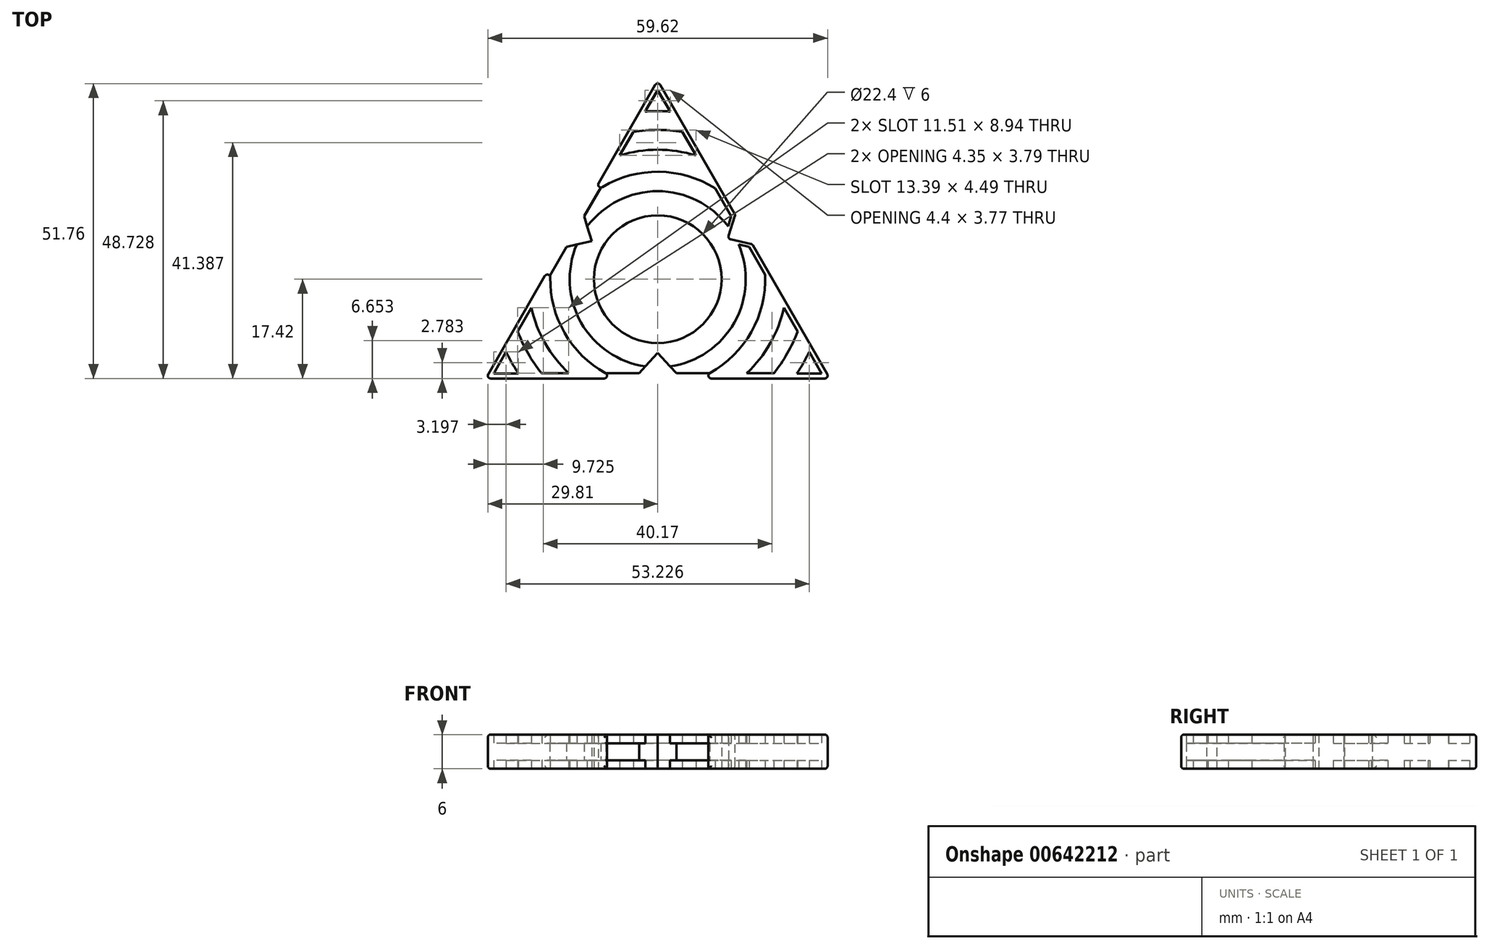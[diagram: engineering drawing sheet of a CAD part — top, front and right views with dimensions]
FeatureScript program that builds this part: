
annotation { "Feature Type Name" : "Feature", "Feature Type Description" : "" }
export const myFeature = defineFeature(function(context is Context, id is Id, definition is map)
    precondition{}
    {
        {
            var Q0;
            Q0=qCreatedBy(makeId("Top.planeOp"),FACE);
            var sketch = newSketch(context, id + "F0", { "sketchPlane" : qUnion([Q0])});
            skPoint(sketch, "E0.0.midPoint", {"position": v(0, -17.42) * mm});
            skLineSegment(sketch, "E1", {"start": v(-12.28, 7.1) * mm, "end": v(-16.57, 6.15) * mm});
            skLineSegment(sketch, "E2", {"start": v(-3.29, -17.42) * mm, "end": v(0, -13.75) * mm});
            skLineSegment(sketch, "E3.MirrorCS", {"start": v(3.29, -17.42) * mm, "end": v(0, -13.75) * mm});
            skLineSegment(sketch, "E4.MirrorCS", {"start": v(-12.28, 7.1) * mm, "end": v(-13.61, 11.27) * mm});
            skLineSegment(sketch, "E5.MirrorCS", {"start": v(12.28, 7.1) * mm, "end": v(16.57, 6.15) * mm});
            skLineSegment(sketch, "E6.MirrorCS", {"start": v(12.28, 7.1) * mm, "end": v(13.61, 11.27) * mm});
            skLineSegment(sketch, "E7", {"start": v(-16.57, 6.15) * mm, "end": v(-30.18, -17.42) * mm});
            skLineSegment(sketch, "E8", {"start": v(-13.61, 11.27) * mm, "end": v(-12.28, 7.1) * mm});
            skLineSegment(sketch, "E9", {"start": v(-16.57, 6.15) * mm, "end": v(-12.28, 7.1) * mm});
            skLineSegment(sketch, "E10", {"start": v(-13.61, 11.27) * mm, "end": v(0, 34.84) * mm});
            skLineSegment(sketch, "E11", {"start": v(0, 34.84) * mm, "end": v(13.61, 11.27) * mm});
            skLineSegment(sketch, "E12", {"start": v(16.57, 6.15) * mm, "end": v(30.18, -17.42) * mm});
            skLineSegment(sketch, "E13", {"start": v(30.18, -17.42) * mm, "end": v(3.29, -17.42) * mm});
            skLineSegment(sketch, "E14", {"start": v(0, -13.75) * mm, "end": v(-3.29, -17.42) * mm});
            skLineSegment(sketch, "E15", {"start": v(-3.29, -17.42) * mm, "end": v(-30.18, -17.42) * mm});
            skCircle(sketch, "E16", {"center": v(0, 0) * mm, "radius": 11.2 * mm});
            skLineSegment(sketch, "E17", {"start": v(-11.57, 6.62) * mm, "end": v(-12.9, 11.08) * mm});
            skLineSegment(sketch, "E18", {"start": v(-12.9, 11.08) * mm, "end": v(0, 33.2) * mm});
            skLineSegment(sketch, "E19.MirrorCS", {"start": v(-11.5, 6.73) * mm, "end": v(-16.03, 5.67) * mm});
            skLineSegment(sketch, "E20.MirrorCS", {"start": v(-16.03, 5.67) * mm, "end": v(-28.79, -16.53) * mm});
            skLineSegment(sketch, "E21", {"start": v(0, -12.94) * mm, "end": v(-3.26, -16.5) * mm});
            skLineSegment(sketch, "E22", {"start": v(-3.26, -16.5) * mm, "end": v(-28.79, -16.53) * mm});
            skLineSegment(sketch, "E23", {"start": v(0, 37.15) * mm, "end": v(0, -20.14) * mm, "construction": true});
            skLineSegment(sketch, "E24.MirrorCS", {"start": v(12.9, 11.08) * mm, "end": v(0, 33.2) * mm});
            skLineSegment(sketch, "E25.MirrorCS", {"start": v(11.57, 6.62) * mm, "end": v(12.9, 11.08) * mm});
            skLineSegment(sketch, "E26.MirrorCS", {"start": v(11.5, 6.73) * mm, "end": v(16.03, 5.67) * mm});
            skLineSegment(sketch, "E27.MirrorCS", {"start": v(16.03, 5.67) * mm, "end": v(28.79, -16.53) * mm});
            skLineSegment(sketch, "E28.MirrorCS", {"start": v(3.26, -16.5) * mm, "end": v(28.79, -16.53) * mm});
            skLineSegment(sketch, "E29.MirrorCS", {"start": v(0, -12.94) * mm, "end": v(3.26, -16.5) * mm});
            skCircle(sketch, "E30", {"center": v(0, 0) * mm, "radius": 15.45 * mm});
            skCircle(sketch, "E31", {"center": v(0, 0) * mm, "radius": 18.86 * mm});
            skCircle(sketch, "E32", {"center": v(0, 0) * mm, "radius": 22.73 * mm});
            skCircle(sketch, "E33", {"center": v(0, 0) * mm, "radius": 26.21 * mm});
            skCircle(sketch, "E34", {"center": v(0, 0) * mm, "radius": 29.5 * mm});
            skSolve(sketch);
        }
        {
            var Q0;
            {var subQ7=sQuery(id+"F0.wireOp",EDGE,"E9");var subQ8=sQuery(id+"F0.wireOp",EDGE,"E7");var subQ9=makeQuery(id+"F0.imprint","INTERSECT",VERTEX,{"derivedFrom":[subQ8,subQ7]});Q0=makeQuery(id+"F0.imprint","IMPRINT",FACE,{"disambiguationData":[TD([[makeQuery(id+"F0.imprint","IMPRINT",EDGE,{"disambiguationData":[TD([[subQ9,-1.0]])],"derivedFrom":subQ8}),1.0]])]});}
            var Q1;
            {var subQ5=sQuery(id+"F0.wireOp",EDGE,"E9");var subQ6=sQuery(id+"F0.wireOp",EDGE,"E8");var subQ7=makeQuery(id+"F0.imprint","INTERSECT",VERTEX,{"derivedFrom":[subQ6,subQ5]});Q1=makeQuery(id+"F0.imprint","IMPRINT",FACE,{"disambiguationData":[TD([[makeQuery(id+"F0.imprint","IMPRINT",EDGE,{"disambiguationData":[TD([[subQ7,1.0]])],"derivedFrom":subQ6}),1.0]])]});}
            var Q2;
            {var subQ6=sQuery(id+"F0.wireOp",EDGE,"E8");var subQ9=sQuery(id+"F0.wireOp",EDGE,"E10");var subQ10=makeQuery(id+"F0.imprint","INTERSECT",VERTEX,{"derivedFrom":[subQ6,subQ9]});Q2=makeQuery(id+"F0.imprint","IMPRINT",FACE,{"disambiguationData":[TD([[makeQuery(id+"F0.imprint","IMPRINT",EDGE,{"disambiguationData":[TD([[subQ10,-1.0]])],"derivedFrom":subQ6}),1.0]])]});}
            var Q3;
            {var subQ0=sQuery(id+"F0.wireOp",EDGE,"E31");var subQ1=sQuery(id+"F0.wireOp",EDGE,"E10");var subQ2=makeQuery(id+"F0.imprint","INTERSECT",VERTEX,{"derivedFrom":[subQ1,subQ0]});Q3=makeQuery(id+"F0.imprint","IMPRINT",FACE,{"disambiguationData":[TD([[makeQuery(id+"F0.imprint","IMPRINT",EDGE,{"disambiguationData":[TD([[subQ2,-1.0]])],"derivedFrom":subQ1}),-1.0]])]});}
            var Q4;
            {var subQ0=sQuery(id+"F0.wireOp",EDGE,"E32");var subQ1=sQuery(id+"F0.wireOp",EDGE,"E10");var subQ2=makeQuery(id+"F0.imprint","INTERSECT",VERTEX,{"derivedFrom":[subQ1,subQ0]});Q4=makeQuery(id+"F0.imprint","IMPRINT",FACE,{"disambiguationData":[TD([[makeQuery(id+"F0.imprint","IMPRINT",EDGE,{"disambiguationData":[TD([[subQ2,-1.0]])],"derivedFrom":subQ1}),-1.0]])]});}
            var Q5;
            {var subQ0=sQuery(id+"F0.wireOp",EDGE,"E34");var subQ1=sQuery(id+"F0.wireOp",EDGE,"E10");var subQ2=makeQuery(id+"F0.imprint","INTERSECT",VERTEX,{"derivedFrom":[subQ1,subQ0]});Q5=makeQuery(id+"F0.imprint","IMPRINT",FACE,{"disambiguationData":[TD([[makeQuery(id+"F0.imprint","IMPRINT",EDGE,{"disambiguationData":[TD([[subQ2,1.0]])],"derivedFrom":subQ1}),-1.0]])]});}
            var Q6;
            {var subQ6=sQuery(id+"F0.wireOp",EDGE,"E11");var subQ7=sQuery(id+"F0.wireOp",EDGE,"E10");var subQ8=makeQuery(id+"F0.imprint","INTERSECT",VERTEX,{"derivedFrom":[subQ7,subQ6]});Q6=makeQuery(id+"F0.imprint","IMPRINT",FACE,{"disambiguationData":[TD([[makeQuery(id+"F0.imprint","IMPRINT",EDGE,{"disambiguationData":[TD([[subQ8,1.0]])],"derivedFrom":subQ7}),-1.0]])]});}
            var Q7;
            {var subQ0=sQuery(id+"F0.wireOp",EDGE,"E34");var subQ1=sQuery(id+"F0.wireOp",EDGE,"E11");var subQ2=makeQuery(id+"F0.imprint","INTERSECT",VERTEX,{"derivedFrom":[subQ1,subQ0]});Q7=makeQuery(id+"F0.imprint","IMPRINT",FACE,{"disambiguationData":[TD([[makeQuery(id+"F0.imprint","IMPRINT",EDGE,{"disambiguationData":[TD([[subQ2,-1.0]])],"derivedFrom":subQ1}),-1.0]])]});}
            var Q8;
            {var subQ0=sQuery(id+"F0.wireOp",EDGE,"E33");var subQ1=sQuery(id+"F0.wireOp",EDGE,"E11");var subQ2=makeQuery(id+"F0.imprint","INTERSECT",VERTEX,{"derivedFrom":[subQ1,subQ0]});Q8=makeQuery(id+"F0.imprint","IMPRINT",FACE,{"disambiguationData":[TD([[makeQuery(id+"F0.imprint","IMPRINT",EDGE,{"disambiguationData":[TD([[subQ2,-1.0]])],"derivedFrom":subQ1}),-1.0]])]});}
            var Q9;
            {var subQ0=sQuery(id+"F0.wireOp",EDGE,"E32");var subQ1=sQuery(id+"F0.wireOp",EDGE,"E11");var subQ2=makeQuery(id+"F0.imprint","INTERSECT",VERTEX,{"derivedFrom":[subQ1,subQ0]});Q9=makeQuery(id+"F0.imprint","IMPRINT",FACE,{"disambiguationData":[TD([[makeQuery(id+"F0.imprint","IMPRINT",EDGE,{"disambiguationData":[TD([[subQ2,-1.0]])],"derivedFrom":subQ1}),-1.0]])]});}
            var Q10;
            {var subQ7=sQuery(id+"F0.wireOp",EDGE,"E11");var subQ8=sQuery(id+"F0.wireOp",EDGE,"E6.MirrorCS");var subQ9=makeQuery(id+"F0.imprint","INTERSECT",VERTEX,{"derivedFrom":[subQ8,subQ7]});Q10=makeQuery(id+"F0.imprint","IMPRINT",FACE,{"disambiguationData":[TD([[makeQuery(id+"F0.imprint","IMPRINT",EDGE,{"disambiguationData":[TD([[subQ9,1.0]])],"derivedFrom":subQ8}),1.0]])]});}
            var Q11;
            {var subQ6=sQuery(id+"F0.wireOp",EDGE,"E6.MirrorCS");var subQ7=sQuery(id+"F0.wireOp",EDGE,"E5.MirrorCS");var subQ8=makeQuery(id+"F0.imprint","INTERSECT",VERTEX,{"derivedFrom":[subQ7,subQ6]});Q11=makeQuery(id+"F0.imprint","IMPRINT",FACE,{"disambiguationData":[TD([[makeQuery(id+"F0.imprint","IMPRINT",EDGE,{"disambiguationData":[TD([[subQ8,-1.0]])],"derivedFrom":subQ7}),-1.0]])]});}
            var Q12;
            {var subQ7=sQuery(id+"F0.wireOp",EDGE,"E12");var subQ8=sQuery(id+"F0.wireOp",EDGE,"E5.MirrorCS");var subQ9=makeQuery(id+"F0.imprint","INTERSECT",VERTEX,{"derivedFrom":[subQ8,subQ7]});Q12=makeQuery(id+"F0.imprint","IMPRINT",FACE,{"disambiguationData":[TD([[makeQuery(id+"F0.imprint","IMPRINT",EDGE,{"disambiguationData":[TD([[subQ9,1.0]])],"derivedFrom":subQ8}),-1.0]])]});}
            var Q13;
            {var subQ0=sQuery(id+"F0.wireOp",EDGE,"E31");var subQ1=sQuery(id+"F0.wireOp",EDGE,"E12");var subQ2=makeQuery(id+"F0.imprint","INTERSECT",VERTEX,{"derivedFrom":[subQ1,subQ0]});Q13=makeQuery(id+"F0.imprint","IMPRINT",FACE,{"disambiguationData":[TD([[makeQuery(id+"F0.imprint","IMPRINT",EDGE,{"disambiguationData":[TD([[subQ2,-1.0]])],"derivedFrom":subQ1}),-1.0]])]});}
            var Q14;
            {var subQ0=sQuery(id+"F0.wireOp",EDGE,"E32");var subQ1=sQuery(id+"F0.wireOp",EDGE,"E12");var subQ2=makeQuery(id+"F0.imprint","INTERSECT",VERTEX,{"derivedFrom":[subQ1,subQ0]});Q14=makeQuery(id+"F0.imprint","IMPRINT",FACE,{"disambiguationData":[TD([[makeQuery(id+"F0.imprint","IMPRINT",EDGE,{"disambiguationData":[TD([[subQ2,-1.0]])],"derivedFrom":subQ1}),-1.0]])]});}
            var Q15;
            {var subQ0=sQuery(id+"F0.wireOp",EDGE,"E34");var subQ1=sQuery(id+"F0.wireOp",EDGE,"E12");var subQ2=makeQuery(id+"F0.imprint","INTERSECT",VERTEX,{"derivedFrom":[subQ1,subQ0]});Q15=makeQuery(id+"F0.imprint","IMPRINT",FACE,{"disambiguationData":[TD([[makeQuery(id+"F0.imprint","IMPRINT",EDGE,{"disambiguationData":[TD([[subQ2,1.0]])],"derivedFrom":subQ1}),-1.0]])]});}
            var Q16;
            {var subQ0=sQuery(id+"F0.wireOp",EDGE,"E13");var subQ1=sQuery(id+"F0.wireOp",EDGE,"E12");var subQ2=makeQuery(id+"F0.imprint","INTERSECT",VERTEX,{"derivedFrom":[subQ1,subQ0]});Q16=makeQuery(id+"F0.imprint","IMPRINT",FACE,{"disambiguationData":[TD([[makeQuery(id+"F0.imprint","IMPRINT",EDGE,{"disambiguationData":[TD([[subQ2,1.0]])],"derivedFrom":subQ1}),-1.0]])]});}
            var Q17;
            {var subQ0=sQuery(id+"F0.wireOp",EDGE,"E34");var subQ1=sQuery(id+"F0.wireOp",EDGE,"E13");var subQ2=makeQuery(id+"F0.imprint","INTERSECT",VERTEX,{"derivedFrom":[subQ1,subQ0]});Q17=makeQuery(id+"F0.imprint","IMPRINT",FACE,{"disambiguationData":[TD([[makeQuery(id+"F0.imprint","IMPRINT",EDGE,{"disambiguationData":[TD([[subQ2,-1.0]])],"derivedFrom":subQ1}),-1.0]])]});}
            var Q18;
            {var subQ0=sQuery(id+"F0.wireOp",EDGE,"E33");var subQ1=sQuery(id+"F0.wireOp",EDGE,"E13");var subQ2=makeQuery(id+"F0.imprint","INTERSECT",VERTEX,{"derivedFrom":[subQ1,subQ0]});Q18=makeQuery(id+"F0.imprint","IMPRINT",FACE,{"disambiguationData":[TD([[makeQuery(id+"F0.imprint","IMPRINT",EDGE,{"disambiguationData":[TD([[subQ2,-1.0]])],"derivedFrom":subQ1}),-1.0]])]});}
            var Q19;
            {var subQ0=sQuery(id+"F0.wireOp",EDGE,"E32");var subQ1=sQuery(id+"F0.wireOp",EDGE,"E13");var subQ2=makeQuery(id+"F0.imprint","INTERSECT",VERTEX,{"derivedFrom":[subQ1,subQ0]});Q19=makeQuery(id+"F0.imprint","IMPRINT",FACE,{"disambiguationData":[TD([[makeQuery(id+"F0.imprint","IMPRINT",EDGE,{"disambiguationData":[TD([[subQ2,-1.0]])],"derivedFrom":subQ1}),-1.0]])]});}
            var Q20;
            {var subQ5=sQuery(id+"F0.wireOp",EDGE,"E3.MirrorCS");var subQ9=sQuery(id+"F0.wireOp",EDGE,"E13");var subQ10=makeQuery(id+"F0.imprint","INTERSECT",VERTEX,{"derivedFrom":[subQ9,subQ5]});Q20=makeQuery(id+"F0.imprint","IMPRINT",FACE,{"disambiguationData":[TD([[makeQuery(id+"F0.imprint","IMPRINT",EDGE,{"disambiguationData":[TD([[subQ10,1.0]])],"derivedFrom":subQ9}),-1.0]])]});}
            var Q21;
            {var subQ6=sQuery(id+"F0.wireOp",EDGE,"E14");var subQ7=sQuery(id+"F0.wireOp",EDGE,"E3.MirrorCS");var subQ8=makeQuery(id+"F0.imprint","INTERSECT",VERTEX,{"derivedFrom":[subQ7,subQ6]});Q21=makeQuery(id+"F0.imprint","IMPRINT",FACE,{"disambiguationData":[TD([[makeQuery(id+"F0.imprint","IMPRINT",EDGE,{"disambiguationData":[TD([[subQ8,1.0]])],"derivedFrom":subQ7}),-1.0]])]});}
            var Q22;
            {var subQ5=sQuery(id+"F0.wireOp",EDGE,"E15");var subQ6=sQuery(id+"F0.wireOp",EDGE,"E14");var subQ7=makeQuery(id+"F0.imprint","INTERSECT",VERTEX,{"derivedFrom":[subQ6,subQ5]});Q22=makeQuery(id+"F0.imprint","IMPRINT",FACE,{"disambiguationData":[TD([[makeQuery(id+"F0.imprint","IMPRINT",EDGE,{"disambiguationData":[TD([[subQ7,1.0]])],"derivedFrom":subQ6}),-1.0]])]});}
            var Q23;
            {var subQ0=sQuery(id+"F0.wireOp",EDGE,"E31");var subQ1=sQuery(id+"F0.wireOp",EDGE,"E15");var subQ2=makeQuery(id+"F0.imprint","INTERSECT",VERTEX,{"derivedFrom":[subQ1,subQ0]});Q23=makeQuery(id+"F0.imprint","IMPRINT",FACE,{"disambiguationData":[TD([[makeQuery(id+"F0.imprint","IMPRINT",EDGE,{"disambiguationData":[TD([[subQ2,-1.0]])],"derivedFrom":subQ1}),-1.0]])]});}
            var Q24;
            {var subQ0=sQuery(id+"F0.wireOp",EDGE,"E32");var subQ1=sQuery(id+"F0.wireOp",EDGE,"E15");var subQ2=makeQuery(id+"F0.imprint","INTERSECT",VERTEX,{"derivedFrom":[subQ1,subQ0]});Q24=makeQuery(id+"F0.imprint","IMPRINT",FACE,{"disambiguationData":[TD([[makeQuery(id+"F0.imprint","IMPRINT",EDGE,{"disambiguationData":[TD([[subQ2,-1.0]])],"derivedFrom":subQ1}),-1.0]])]});}
            var Q25;
            {var subQ5=sQuery(id+"F0.wireOp",EDGE,"E15");var subQ6=sQuery(id+"F0.wireOp",EDGE,"E7");var subQ7=makeQuery(id+"F0.imprint","INTERSECT",VERTEX,{"derivedFrom":[subQ6,subQ5]});Q25=makeQuery(id+"F0.imprint","IMPRINT",FACE,{"disambiguationData":[TD([[makeQuery(id+"F0.imprint","IMPRINT",EDGE,{"disambiguationData":[TD([[subQ7,1.0]])],"derivedFrom":subQ6}),1.0]])]});}
            var Q26;
            {var subQ0=sQuery(id+"F0.wireOp",EDGE,"E34");var subQ1=sQuery(id+"F0.wireOp",EDGE,"E15");var subQ2=makeQuery(id+"F0.imprint","INTERSECT",VERTEX,{"derivedFrom":[subQ1,subQ0]});Q26=makeQuery(id+"F0.imprint","IMPRINT",FACE,{"disambiguationData":[TD([[makeQuery(id+"F0.imprint","IMPRINT",EDGE,{"disambiguationData":[TD([[subQ2,1.0]])],"derivedFrom":subQ1}),-1.0]])]});}
            var Q27;
            {var subQ0=sQuery(id+"F0.wireOp",EDGE,"E34");var subQ1=sQuery(id+"F0.wireOp",EDGE,"E7");var subQ2=makeQuery(id+"F0.imprint","INTERSECT",VERTEX,{"derivedFrom":[subQ1,subQ0]});Q27=makeQuery(id+"F0.imprint","IMPRINT",FACE,{"disambiguationData":[TD([[makeQuery(id+"F0.imprint","IMPRINT",EDGE,{"disambiguationData":[TD([[subQ2,1.0]])],"derivedFrom":subQ1}),1.0]])]});}
            var Q28;
            {var subQ0=sQuery(id+"F0.wireOp",EDGE,"E32");var subQ1=sQuery(id+"F0.wireOp",EDGE,"E7");var subQ2=makeQuery(id+"F0.imprint","INTERSECT",VERTEX,{"derivedFrom":[subQ1,subQ0]});Q28=makeQuery(id+"F0.imprint","IMPRINT",FACE,{"disambiguationData":[TD([[makeQuery(id+"F0.imprint","IMPRINT",EDGE,{"disambiguationData":[TD([[subQ2,-1.0]])],"derivedFrom":subQ1}),1.0]])]});}
            var Q29;
            {var subQ0=sQuery(id+"F0.wireOp",EDGE,"E31");var subQ1=sQuery(id+"F0.wireOp",EDGE,"E7");var subQ2=makeQuery(id+"F0.imprint","INTERSECT",VERTEX,{"derivedFrom":[subQ1,subQ0]});Q29=makeQuery(id+"F0.imprint","IMPRINT",FACE,{"disambiguationData":[TD([[makeQuery(id+"F0.imprint","IMPRINT",EDGE,{"disambiguationData":[TD([[subQ2,-1.0]])],"derivedFrom":subQ1}),1.0]])]});}
            var Q30;
            Q30=makeQuery(id+"F0.imprint","IMPRINT",FACE,{"disambiguationData":[TD([[makeQuery(id+"F0.imprint","IMPRINT",EDGE,{"derivedFrom":sQuery(id+"F0.wireOp",EDGE,"E16")}),-1.0]])]});
            var Q31;
            {var subQ0=sQuery(id+"F0.wireOp",EDGE,"E31");var subQ1=sQuery(id+"F0.wireOp",EDGE,"E18");var subQ2=makeQuery(id+"F0.imprint","INTERSECT",VERTEX,{"derivedFrom":[subQ1,subQ0]});Q31=makeQuery(id+"F0.imprint","IMPRINT",FACE,{"disambiguationData":[TD([[makeQuery(id+"F0.imprint","IMPRINT",EDGE,{"disambiguationData":[TD([[subQ2,-1.0]])],"derivedFrom":subQ1}),-1.0]])]});}
            var Q32;
            {var subQ0=sQuery(id+"F0.wireOp",EDGE,"E33");var subQ1=sQuery(id+"F0.wireOp",EDGE,"E18");var subQ2=makeQuery(id+"F0.imprint","INTERSECT",VERTEX,{"derivedFrom":[subQ1,subQ0]});Q32=makeQuery(id+"F0.imprint","IMPRINT",FACE,{"disambiguationData":[TD([[makeQuery(id+"F0.imprint","IMPRINT",EDGE,{"disambiguationData":[TD([[subQ2,-1.0]])],"derivedFrom":subQ1}),-1.0]])]});}
            var Q33;
            {var subQ0=sQuery(id+"F0.wireOp",EDGE,"E31");var subQ1=sQuery(id+"F0.wireOp",EDGE,"E27.MirrorCS");var subQ2=makeQuery(id+"F0.imprint","INTERSECT",VERTEX,{"derivedFrom":[subQ1,subQ0]});Q33=makeQuery(id+"F0.imprint","IMPRINT",FACE,{"disambiguationData":[TD([[makeQuery(id+"F0.imprint","IMPRINT",EDGE,{"disambiguationData":[TD([[subQ2,-1.0]])],"derivedFrom":subQ1}),-1.0]])]});}
            var Q34;
            {var subQ0=sQuery(id+"F0.wireOp",EDGE,"E33");var subQ1=sQuery(id+"F0.wireOp",EDGE,"E27.MirrorCS");var subQ2=makeQuery(id+"F0.imprint","INTERSECT",VERTEX,{"derivedFrom":[subQ1,subQ0]});Q34=makeQuery(id+"F0.imprint","IMPRINT",FACE,{"disambiguationData":[TD([[makeQuery(id+"F0.imprint","IMPRINT",EDGE,{"disambiguationData":[TD([[subQ2,-1.0]])],"derivedFrom":subQ1}),-1.0]])]});}
            var Q35;
            {var subQ0=sQuery(id+"F0.wireOp",EDGE,"E31");var subQ1=sQuery(id+"F0.wireOp",EDGE,"E20.MirrorCS");var subQ2=makeQuery(id+"F0.imprint","INTERSECT",VERTEX,{"derivedFrom":[subQ1,subQ0]});Q35=makeQuery(id+"F0.imprint","IMPRINT",FACE,{"disambiguationData":[TD([[makeQuery(id+"F0.imprint","IMPRINT",EDGE,{"disambiguationData":[TD([[subQ2,-1.0]])],"derivedFrom":subQ1}),1.0]])]});}
            var Q36;
            {var subQ0=sQuery(id+"F0.wireOp",EDGE,"E33");var subQ1=sQuery(id+"F0.wireOp",EDGE,"E20.MirrorCS");var subQ2=makeQuery(id+"F0.imprint","INTERSECT",VERTEX,{"derivedFrom":[subQ1,subQ0]});Q36=makeQuery(id+"F0.imprint","IMPRINT",FACE,{"disambiguationData":[TD([[makeQuery(id+"F0.imprint","IMPRINT",EDGE,{"disambiguationData":[TD([[subQ2,-1.0]])],"derivedFrom":subQ1}),1.0]])]});}
            extrude(context, id + "F1", {"entities" : qUnion([Q0, Q1, Q2, Q3, Q4, Q5, Q6, Q7, Q8, Q9, Q10, Q11, Q12, Q13, Q14, Q15, Q16, Q17, Q18, Q19, Q20, Q21, Q22, Q23, Q24, Q25, Q26, Q27, Q28, Q29, Q30, Q31, Q32, Q33, Q34, Q35, Q36]), "depth" : 6 * mm, "offsetDistance" : 25.4 * mm, "symmetric" : true});
        }
        {
            var Q0;
            {var subQ0=sQuery(id+"F0.wireOp",EDGE,"E22");var subQ1=sQuery(id+"F0.wireOp",EDGE,"E20.MirrorCS");var subQ2=makeQuery(id+"F0.imprint","INTERSECT",VERTEX,{"derivedFrom":[subQ1,subQ0]});Q0=makeQuery(id+"F0.imprint","IMPRINT",FACE,{"disambiguationData":[TD([[makeQuery(id+"F0.imprint","IMPRINT",EDGE,{"disambiguationData":[TD([[subQ2,1.0]])],"derivedFrom":subQ1}),1.0]])]});}
            var Q1;
            {var subQ0=sQuery(id+"F0.wireOp",EDGE,"E32");var subQ1=sQuery(id+"F0.wireOp",EDGE,"E20.MirrorCS");var subQ2=makeQuery(id+"F0.imprint","INTERSECT",VERTEX,{"derivedFrom":[subQ1,subQ0]});Q1=makeQuery(id+"F0.imprint","IMPRINT",FACE,{"disambiguationData":[TD([[makeQuery(id+"F0.imprint","IMPRINT",EDGE,{"disambiguationData":[TD([[subQ2,-1.0]])],"derivedFrom":subQ1}),1.0]])]});}
            var Q2;
            {var subQ6=sQuery(id+"F0.wireOp",EDGE,"E19.MirrorCS");var subQ9=sQuery(id+"F0.wireOp",EDGE,"E20.MirrorCS");var subQ10=makeQuery(id+"F0.imprint","INTERSECT",VERTEX,{"derivedFrom":[subQ6,subQ9]});Q2=makeQuery(id+"F0.imprint","IMPRINT",FACE,{"disambiguationData":[TD([[makeQuery(id+"F0.imprint","IMPRINT",EDGE,{"disambiguationData":[TD([[subQ10,1.0]])],"derivedFrom":subQ6}),1.0]])]});}
            var Q3;
            {var subQ5=sQuery(id+"F0.wireOp",EDGE,"E27.MirrorCS");var subQ6=sQuery(id+"F0.wireOp",EDGE,"E26.MirrorCS");var subQ7=makeQuery(id+"F0.imprint","INTERSECT",VERTEX,{"derivedFrom":[subQ6,subQ5]});Q3=makeQuery(id+"F0.imprint","IMPRINT",FACE,{"disambiguationData":[TD([[makeQuery(id+"F0.imprint","IMPRINT",EDGE,{"disambiguationData":[TD([[subQ7,1.0]])],"derivedFrom":subQ6}),-1.0]])]});}
            var Q4;
            {var subQ0=sQuery(id+"F0.wireOp",EDGE,"E32");var subQ1=sQuery(id+"F0.wireOp",EDGE,"E27.MirrorCS");var subQ2=makeQuery(id+"F0.imprint","INTERSECT",VERTEX,{"derivedFrom":[subQ1,subQ0]});Q4=makeQuery(id+"F0.imprint","IMPRINT",FACE,{"disambiguationData":[TD([[makeQuery(id+"F0.imprint","IMPRINT",EDGE,{"disambiguationData":[TD([[subQ2,-1.0]])],"derivedFrom":subQ1}),-1.0]])]});}
            var Q5;
            {var subQ5=sQuery(id+"F0.wireOp",EDGE,"E18");var subQ6=sQuery(id+"F0.wireOp",EDGE,"E17");var subQ7=makeQuery(id+"F0.imprint","INTERSECT",VERTEX,{"derivedFrom":[subQ6,subQ5]});Q5=makeQuery(id+"F0.imprint","IMPRINT",FACE,{"disambiguationData":[TD([[makeQuery(id+"F0.imprint","IMPRINT",EDGE,{"disambiguationData":[TD([[subQ7,1.0]])],"derivedFrom":subQ6}),-1.0]])]});}
            var Q6;
            {var subQ0=sQuery(id+"F0.wireOp",EDGE,"E32");var subQ1=sQuery(id+"F0.wireOp",EDGE,"E18");var subQ2=makeQuery(id+"F0.imprint","INTERSECT",VERTEX,{"derivedFrom":[subQ1,subQ0]});Q6=makeQuery(id+"F0.imprint","IMPRINT",FACE,{"disambiguationData":[TD([[makeQuery(id+"F0.imprint","IMPRINT",EDGE,{"disambiguationData":[TD([[subQ2,-1.0]])],"derivedFrom":subQ1}),-1.0]])]});}
            var Q7;
            {var subQ0=sQuery(id+"F0.wireOp",EDGE,"E24.MirrorCS");var subQ1=sQuery(id+"F0.wireOp",EDGE,"E18");var subQ2=makeQuery(id+"F0.imprint","INTERSECT",VERTEX,{"derivedFrom":[subQ1,subQ0]});Q7=makeQuery(id+"F0.imprint","IMPRINT",FACE,{"disambiguationData":[TD([[makeQuery(id+"F0.imprint","IMPRINT",EDGE,{"disambiguationData":[TD([[subQ2,1.0]])],"derivedFrom":subQ1}),-1.0]])]});}
            var Q8;
            {var subQ0=sQuery(id+"F0.wireOp",EDGE,"E28.MirrorCS");var subQ1=sQuery(id+"F0.wireOp",EDGE,"E27.MirrorCS");var subQ2=makeQuery(id+"F0.imprint","INTERSECT",VERTEX,{"derivedFrom":[subQ1,subQ0]});Q8=makeQuery(id+"F0.imprint","IMPRINT",FACE,{"disambiguationData":[TD([[makeQuery(id+"F0.imprint","IMPRINT",EDGE,{"disambiguationData":[TD([[subQ2,1.0]])],"derivedFrom":subQ1}),-1.0]])]});}
            extrude(context, id + "F2", {"entities" : qUnion([Q0, Q1, Q2, Q3, Q4, Q5, Q6, Q7, Q8]), "operationType" : NewBodyOperationType.ADD, "depth" : 3 * mm, "offsetDistance" : 25.4 * mm, "symmetric" : true});
        }
        {
            var Q0;
            Q0=makeQuery(id+"F1.opExtrude","CAP_EDGE",EDGE,{"disambiguationData":[OSD([sQuery(id+"F0.wireOp",EDGE,"E15")])],"isStart":false});
            var Q1;
            Q1=makeQuery(id+"F1.opExtrude","CAP_EDGE",EDGE,{"disambiguationData":[OSD([sQuery(id+"F0.wireOp",EDGE,"E12")])],"isStart":false});
            var Q2;
            Q2=makeQuery(id+"F1.opExtrude","CAP_EDGE",EDGE,{"disambiguationData":[OSD([sQuery(id+"F0.wireOp",EDGE,"E11")])],"isStart":false});
            var Q3;
            Q3=makeQuery(id+"F1.opExtrude","CAP_EDGE",EDGE,{"disambiguationData":[OSD([sQuery(id+"F0.wireOp",EDGE,"E10")])],"isStart":false});
            var Q4;
            Q4=makeQuery(id+"F1.opExtrude","CAP_EDGE",EDGE,{"disambiguationData":[OSD([sQuery(id+"F0.wireOp",EDGE,"E9")])],"isStart":false});
            var Q5;
            Q5=makeQuery(id+"F1.opExtrude","CAP_EDGE",EDGE,{"disambiguationData":[OSD([sQuery(id+"F0.wireOp",EDGE,"E8")])],"isStart":false});
            var Q6;
            Q6=makeQuery(id+"F1.opExtrude","CAP_EDGE",EDGE,{"disambiguationData":[OSD([sQuery(id+"F0.wireOp",EDGE,"E6.MirrorCS")])],"isStart":false});
            var Q7;
            Q7=makeQuery(id+"F1.opExtrude","CAP_EDGE",EDGE,{"disambiguationData":[OSD([sQuery(id+"F0.wireOp",EDGE,"E5.MirrorCS")])],"isStart":false});
            var Q8;
            Q8=makeQuery(id+"F1.opExtrude","CAP_EDGE",EDGE,{"disambiguationData":[OSD([sQuery(id+"F0.wireOp",EDGE,"E14")])],"isStart":false});
            var Q9;
            Q9=makeQuery(id+"F1.opExtrude","CAP_EDGE",EDGE,{"disambiguationData":[OSD([sQuery(id+"F0.wireOp",EDGE,"E3.MirrorCS")])],"isStart":false});
            var Q10;
            Q10=makeQuery(id+"F1.opExtrude","CAP_EDGE",EDGE,{"disambiguationData":[OSD([sQuery(id+"F0.wireOp",EDGE,"E13")])],"isStart":false});
            var Q11;
            Q11=makeQuery(id+"F1.opExtrude","CAP_EDGE",EDGE,{"disambiguationData":[OSD([sQuery(id+"F0.wireOp",EDGE,"E7")])],"isStart":false});
            var Q12;
            Q12=makeQuery(id+"F1.opExtrude","CAP_EDGE",EDGE,{"disambiguationData":[OSD([sQuery(id+"F0.wireOp",EDGE,"E15")])],"isStart":true});
            var Q13;
            Q13=makeQuery(id+"F1.opExtrude","CAP_EDGE",EDGE,{"disambiguationData":[OSD([sQuery(id+"F0.wireOp",EDGE,"E14")])],"isStart":true});
            var Q14;
            Q14=makeQuery(id+"F1.opExtrude","CAP_EDGE",EDGE,{"disambiguationData":[OSD([sQuery(id+"F0.wireOp",EDGE,"E3.MirrorCS")])],"isStart":true});
            var Q15;
            Q15=makeQuery(id+"F1.opExtrude","CAP_EDGE",EDGE,{"disambiguationData":[OSD([sQuery(id+"F0.wireOp",EDGE,"E13")])],"isStart":true});
            var Q16;
            Q16=makeQuery(id+"F1.opExtrude","CAP_EDGE",EDGE,{"disambiguationData":[OSD([sQuery(id+"F0.wireOp",EDGE,"E12")])],"isStart":true});
            var Q17;
            Q17=makeQuery(id+"F1.opExtrude","CAP_EDGE",EDGE,{"disambiguationData":[OSD([sQuery(id+"F0.wireOp",EDGE,"E11")])],"isStart":true});
            var Q18;
            Q18=makeQuery(id+"F1.opExtrude","CAP_EDGE",EDGE,{"disambiguationData":[OSD([sQuery(id+"F0.wireOp",EDGE,"E10")])],"isStart":true});
            var Q19;
            Q19=makeQuery(id+"F1.opExtrude","CAP_EDGE",EDGE,{"disambiguationData":[OSD([sQuery(id+"F0.wireOp",EDGE,"E7")])],"isStart":true});
            var Q20;
            Q20=makeQuery(id+"F1.opExtrude","CAP_EDGE",EDGE,{"disambiguationData":[OSD([sQuery(id+"F0.wireOp",EDGE,"E9")])],"isStart":true});
            var Q21;
            Q21=makeQuery(id+"F1.opExtrude","CAP_EDGE",EDGE,{"disambiguationData":[OSD([sQuery(id+"F0.wireOp",EDGE,"E8")])],"isStart":true});
            var Q22;
            Q22=makeQuery(id+"F1.opExtrude","CAP_EDGE",EDGE,{"disambiguationData":[OSD([sQuery(id+"F0.wireOp",EDGE,"E6.MirrorCS")])],"isStart":true});
            var Q23;
            Q23=makeQuery(id+"F1.opExtrude","CAP_EDGE",EDGE,{"disambiguationData":[OSD([sQuery(id+"F0.wireOp",EDGE,"E5.MirrorCS")])],"isStart":true});
            var Q24;
            Q24=makeQuery(id+"F1.opExtrude","SWEPT_EDGE",EDGE,{"disambiguationData":[OSD([sQuery(id+"F0.wireOp",EDGE,"E14"),sQuery(id+"F0.wireOp",EDGE,"E15")])]});
            var Q25;
            Q25=makeQuery(id+"F1.opExtrude","SWEPT_EDGE",EDGE,{"disambiguationData":[OSD([sQuery(id+"F0.wireOp",EDGE,"E3.MirrorCS"),sQuery(id+"F0.wireOp",EDGE,"E14")])]});
            var Q26;
            Q26=makeQuery(id+"F1.opExtrude","SWEPT_EDGE",EDGE,{"disambiguationData":[OSD([sQuery(id+"F0.wireOp",EDGE,"E13"),sQuery(id+"F0.wireOp",EDGE,"E3.MirrorCS")])]});
            var Q27;
            Q27=makeQuery(id+"F1.opExtrude","SWEPT_EDGE",EDGE,{"disambiguationData":[OSD([sQuery(id+"F0.wireOp",EDGE,"E12"),sQuery(id+"F0.wireOp",EDGE,"E13")])]});
            var Q28;
            Q28=makeQuery(id+"F1.opExtrude","SWEPT_EDGE",EDGE,{"disambiguationData":[OSD([sQuery(id+"F0.wireOp",EDGE,"E5.MirrorCS"),sQuery(id+"F0.wireOp",EDGE,"E6.MirrorCS")])]});
            var Q29;
            Q29=makeQuery(id+"F1.opExtrude","SWEPT_EDGE",EDGE,{"disambiguationData":[OSD([sQuery(id+"F0.wireOp",EDGE,"E5.MirrorCS"),sQuery(id+"F0.wireOp",EDGE,"E12")])]});
            var Q30;
            Q30=makeQuery(id+"F1.opExtrude","SWEPT_EDGE",EDGE,{"disambiguationData":[OSD([sQuery(id+"F0.wireOp",EDGE,"E6.MirrorCS"),sQuery(id+"F0.wireOp",EDGE,"E11")])]});
            var Q31;
            Q31=makeQuery(id+"F1.opExtrude","SWEPT_EDGE",EDGE,{"disambiguationData":[OSD([sQuery(id+"F0.wireOp",EDGE,"E10"),sQuery(id+"F0.wireOp",EDGE,"E11")])]});
            var Q32;
            Q32=makeQuery(id+"F1.opExtrude","SWEPT_EDGE",EDGE,{"disambiguationData":[OSD([sQuery(id+"F0.wireOp",EDGE,"E8"),sQuery(id+"F0.wireOp",EDGE,"E9")])]});
            var Q33;
            Q33=makeQuery(id+"F1.opExtrude","SWEPT_EDGE",EDGE,{"disambiguationData":[OSD([sQuery(id+"F0.wireOp",EDGE,"E7"),sQuery(id+"F0.wireOp",EDGE,"E9")])]});
            var Q34;
            Q34=makeQuery(id+"F1.opExtrude","SWEPT_EDGE",EDGE,{"disambiguationData":[OSD([sQuery(id+"F0.wireOp",EDGE,"E8"),sQuery(id+"F0.wireOp",EDGE,"E10")])]});
            var Q35;
            Q35=makeQuery(id+"F1.opExtrude","SWEPT_EDGE",EDGE,{"disambiguationData":[OSD([sQuery(id+"F0.wireOp",EDGE,"E7"),sQuery(id+"F0.wireOp",EDGE,"E15")])]});
            fillet(context, id + "F3", {"entities" : qUnion([Q0, Q1, Q2, Q3, Q4, Q5, Q6, Q7, Q8, Q9, Q10, Q11, Q12, Q13, Q14, Q15, Q16, Q17, Q18, Q19, Q20, Q21, Q22, Q23, Q24, Q25, Q26, Q27, Q28, Q29, Q30, Q31, Q32, Q33, Q34, Q35]), "radius" : .5 * mm, "tangentPropagation" : true, "allowEdgeOverflow" : false});
        }
    });
